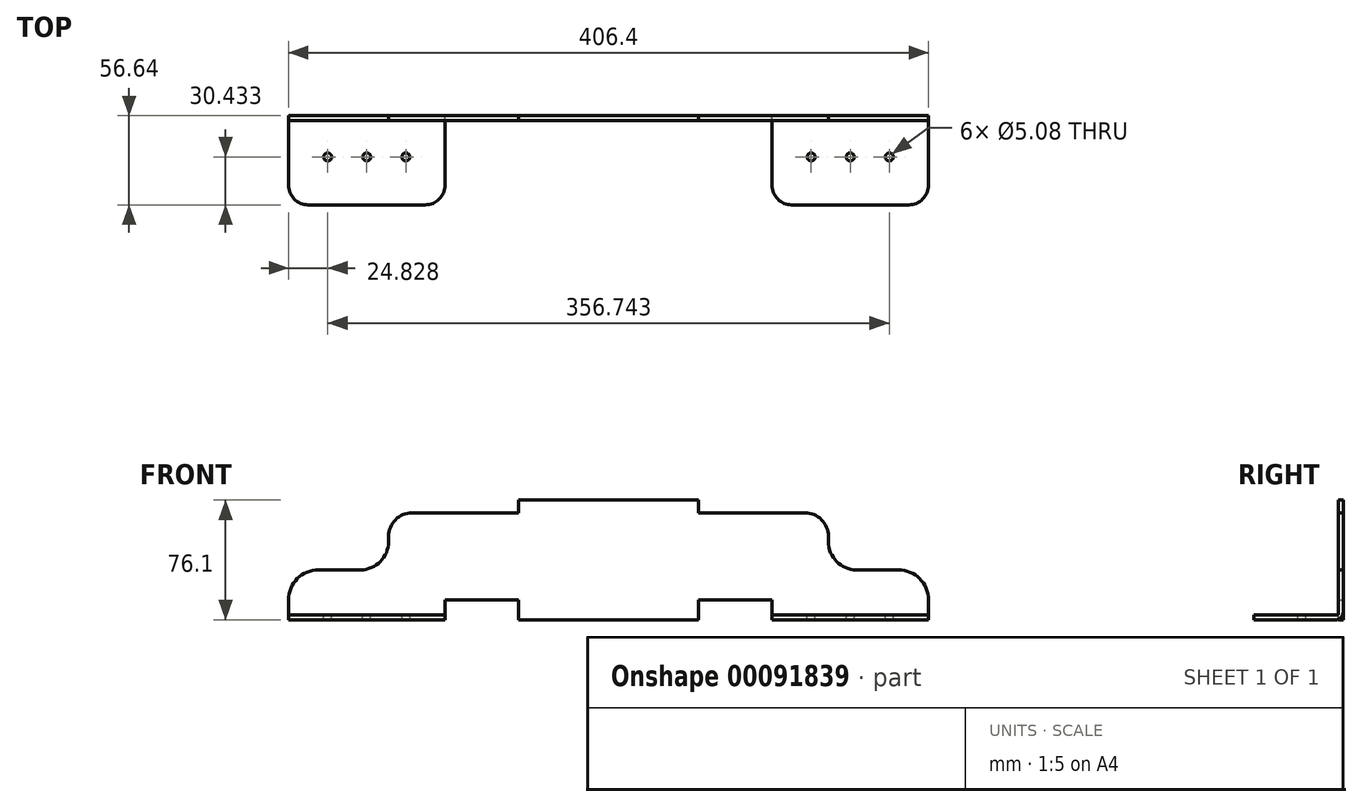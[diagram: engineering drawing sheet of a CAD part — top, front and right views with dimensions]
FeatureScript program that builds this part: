
annotation { "Feature Type Name" : "Feature", "Feature Type Description" : "" }
export const myFeature = defineFeature(function(context is Context, id is Id, definition is map)
    precondition{}
    {
        {
            var Q0;
            Q0=qCreatedBy(makeId("Front.planeOp"),FACE);
            var sketch = newSketch(context, id + "F0", { "sketchPlane" : qUnion([Q0])});
            skLineSegment(sketch, "E0.bottom", {"start": v(0, 0) * mm, "end": v(-57.15, 0) * mm});
            skLineSegment(sketch, "E0.top", {"start": v(0, 40.34) * mm, "end": v(-57.15, 40.34) * mm});
            skLineSegment(sketch, "E0.left", {"start": v(0, 0) * mm, "end": v(0, 40.34) * mm});
            skLineSegment(sketch, "E0.right", {"start": v(-57.15, 0) * mm, "end": v(-57.15, 40.34) * mm});
            skLineSegment(sketch, "E1.bottom", {"start": v(-57.15, 40.34) * mm, "end": v(-103.89, 40.34) * mm});
            skLineSegment(sketch, "E1.top", {"start": v(-57.15, 12.7) * mm, "end": v(-103.89, 12.7) * mm});
            skLineSegment(sketch, "E1.left", {"start": v(-57.15, 40.34) * mm, "end": v(-57.15, 12.7) * mm});
            skLineSegment(sketch, "E1.right", {"start": v(-103.89, 40.34) * mm, "end": v(-103.89, 12.7) * mm});
            skLineSegment(sketch, "E2.MirrorCS", {"start": v(-103.89, 40.34) * mm, "end": v(-103.89, 67.97) * mm});
            skLineSegment(sketch, "E3.MirrorCS", {"start": v(-57.15, 67.97) * mm, "end": v(-103.89, 67.97) * mm});
            skLineSegment(sketch, "E4.MirrorCS", {"start": v(-57.15, 40.34) * mm, "end": v(-57.15, 67.97) * mm});
            skLineSegment(sketch, "E5.bottom", {"start": v(-103.89, 67.97) * mm, "end": v(-139.7, 67.97) * mm});
            skLineSegment(sketch, "E5.top", {"start": v(-103.89, 0) * mm, "end": v(-139.7, 0) * mm});
            skLineSegment(sketch, "E5.left", {"start": v(-103.89, 67.97) * mm, "end": v(-103.89, 0) * mm});
            skLineSegment(sketch, "E6.bottom", {"start": v(-139.7, 0) * mm, "end": v(-203.2, 0) * mm});
            skLineSegment(sketch, "E6.top", {"start": v(-139.7, 31.75) * mm, "end": v(-203.2, 31.75) * mm});
            skLineSegment(sketch, "E6.left", {"start": v(-139.7, 0) * mm, "end": v(-139.7, 31.75) * mm});
            skLineSegment(sketch, "E6.right", {"start": v(-203.2, 0) * mm, "end": v(-203.2, 31.75) * mm});
            skLineSegment(sketch, "E7", {"start": v(-57.15, 67.97) * mm, "end": v(0, 67.97) * mm});
            skLineSegment(sketch, "E8", {"start": v(0, 67.97) * mm, "end": v(0, 40.34) * mm});
            skLineSegment(sketch, "E9", {"start": v(-57.15, 67.97) * mm, "end": v(-57.15, 76.1) * mm});
            skLineSegment(sketch, "E10", {"start": v(-57.15, 76.1) * mm, "end": v(0, 76.1) * mm});
            skLineSegment(sketch, "E11", {"start": v(0, 76.1) * mm, "end": v(0, 67.97) * mm});
            skLineSegment(sketch, "E12", {"start": v(-139.7, 67.97) * mm, "end": v(-139.7, 31.75) * mm});
            skLineSegment(sketch, "E13", {"start": v(-103.89, 3.18) * mm, "end": v(-203.2, 3.18) * mm});
            skLineSegment(sketch, "E14", {"start": v(-203.2, 3.18) * mm, "end": v(-203.2, 0) * mm});
            skSolve(sketch);
        }
        {
            var Q0;
            {var subQ0=sQuery(id+"F0.wireOp",EDGE,"E6.top");Q0=makeQuery(id+"F0.imprint","IMPRINT",FACE,{"disambiguationData":[TD([[makeQuery(id+"F0.imprint","IMPRINT",EDGE,{"derivedFrom":subQ0}),1.0]])]});}
            var Q1;
            {var subQ0=sQuery(id+"F0.wireOp",EDGE,"2503e86a-e470-4966-b1d1-eb231d9cc19f15.MirrorCS");Q1=makeQuery(id+"F0.imprint","IMPRINT",FACE,{"disambiguationData":[TD([[makeQuery(id+"F0.imprint","IMPRINT",EDGE,{"derivedFrom":subQ0}),-1.0]])]});}
            var Q2;
            Q2=makeQuery(id+"F0.imprint","IMPRINT",FACE,{"disambiguationData":[TD([[makeQuery(id+"F0.imprint","IMPRINT",EDGE,{"derivedFrom":sQuery(id+"F0.wireOp",EDGE,"E0.bottom")}),-1.0]])]});
            var Q3;
            {var subQ0=sQuery(id+"F0.wireOp",EDGE,"E1.bottom");Q3=makeQuery(id+"F0.imprint","IMPRINT",FACE,{"disambiguationData":[TD([[makeQuery(id+"F0.imprint","IMPRINT",EDGE,{"derivedFrom":subQ0}),1.0]])]});}
            var Q4;
            {var subQ0=sQuery(id+"F0.wireOp",EDGE,"E1.bottom");Q4=makeQuery(id+"F0.imprint","IMPRINT",FACE,{"disambiguationData":[TD([[makeQuery(id+"F0.imprint","IMPRINT",EDGE,{"derivedFrom":subQ0}),-1.0]])]});}
            var Q5;
            Q5=makeQuery(id+"F0.imprint","IMPRINT",FACE,{"disambiguationData":[TD([[makeQuery(id+"F0.imprint","IMPRINT",EDGE,{"derivedFrom":sQuery(id+"F0.wireOp",EDGE,"d7e3aea6-42ce-4507-9b3a-23066b92194c1.MirrorCS")}),-1.0]])]});
            var Q6;
            Q6=makeQuery(id+"F0.imprint","IMPRINT",FACE,{"disambiguationData":[TD([[makeQuery(id+"F0.imprint","IMPRINT",EDGE,{"derivedFrom":sQuery(id+"F0.wireOp",EDGE,"d7e3aea6-42ce-4507-9b3a-23066b92194c1.MirrorCS")}),1.0]])]});
            var Q7;
            Q7=makeQuery(id+"F0.imprint","IMPRINT",FACE,{"disambiguationData":[TD([[makeQuery(id+"F0.imprint","IMPRINT",EDGE,{"derivedFrom":sQuery(id+"F0.wireOp",EDGE,"2503e86a-e470-4966-b1d1-eb231d9cc19f5.MirrorCS")}),1.0]])]});
            var Q8;
            {var subQ0=sQuery(id+"F0.wireOp",EDGE,"2503e86a-e470-4966-b1d1-eb231d9cc19f10.MirrorCS");Q8=makeQuery(id+"F0.imprint","IMPRINT",FACE,{"disambiguationData":[TD([[makeQuery(id+"F0.imprint","IMPRINT",EDGE,{"derivedFrom":subQ0}),-1.0]])]});}
            var Q9;
            Q9=makeQuery(id+"F0.imprint","IMPRINT",FACE,{"disambiguationData":[TD([[makeQuery(id+"F0.imprint","IMPRINT",EDGE,{"derivedFrom":sQuery(id+"F0.wireOp",EDGE,"2503e86a-e470-4966-b1d1-eb231d9cc19f17.MirrorCS")}),-1.0]])]});
            var Q10;
            {var subQ8=sQuery(id+"F0.wireOp",EDGE,"E5.bottom");Q10=makeQuery(id+"F0.imprint","IMPRINT",FACE,{"disambiguationData":[TD([[makeQuery(id+"F0.imprint","IMPRINT",EDGE,{"derivedFrom":subQ8}),1.0]])]});}
            var Q11;
            {var subQ5=sQuery(id+"F0.wireOp",EDGE,"2503e86a-e470-4966-b1d1-eb231d9cc19f8.MirrorCS");Q11=makeQuery(id+"F0.imprint","IMPRINT",FACE,{"disambiguationData":[TD([[makeQuery(id+"F0.imprint","IMPRINT",EDGE,{"derivedFrom":subQ5}),-1.0]])]});}
            var Q12;
            Q12=makeQuery(id+"F0.imprint","IMPRINT",FACE,{"disambiguationData":[TD([[makeQuery(id+"F0.imprint","IMPRINT",EDGE,{"derivedFrom":sQuery(id+"F0.wireOp",EDGE,"E0.top")}),-1.0]])]});
            var Q13;
            Q13=makeQuery(id+"F0.imprint","IMPRINT",FACE,{"disambiguationData":[TD([[makeQuery(id+"F0.imprint","IMPRINT",EDGE,{"derivedFrom":sQuery(id+"F0.wireOp",EDGE,"E7")}),1.0]])]});
            extrude(context, id + "F1", {"entities" : qUnion([Q0, Q1, Q2, Q3, Q4, Q5, Q6, Q7, Q8, Q9, Q10, Q11, Q12, Q13]), "depth" : 3.17 * mm});
        }
        {
            var Q0;
            {var subQ5=sQuery(id+"F0.wireOp",EDGE,"5YBeUyX7-qxhe-6PBE-ShX0-8MnYnTLxuj8z.left");Q0=makeQuery(id+"F0.imprint","IMPRINT",FACE,{"disambiguationData":[TD([[makeQuery(id+"F0.imprint","IMPRINT",EDGE,{"derivedFrom":subQ5}),-1.0]])]});}
            var Q1;
            {var subQ5=sQuery(id+"F0.wireOp",EDGE,"5YBeUyX7-qxhe-6PBE-ShX0-8MnYnTLxuj8z.right");Q1=makeQuery(id+"F0.imprint","IMPRINT",FACE,{"disambiguationData":[TD([[makeQuery(id+"F0.imprint","IMPRINT",EDGE,{"derivedFrom":subQ5}),1.0]])]});}
            var Q2;
            {var subQ0=sQuery(id+"F0.wireOp",EDGE,"2503e86a-e470-4966-b1d1-eb231d9cc19f11.MirrorCS");Q2=makeQuery(id+"F0.imprint","IMPRINT",FACE,{"disambiguationData":[TD([[makeQuery(id+"F0.imprint","IMPRINT",EDGE,{"derivedFrom":subQ0}),-1.0]])]});}
            var Q3;
            {var subQ0=sQuery(id+"F0.wireOp",EDGE,"2503e86a-e470-4966-b1d1-eb231d9cc19f18.MirrorCS");Q3=makeQuery(id+"F0.imprint","IMPRINT",FACE,{"disambiguationData":[TD([[makeQuery(id+"F0.imprint","IMPRINT",EDGE,{"derivedFrom":subQ0}),1.0]])]});}
            var Q4;
            {var subQ0=sQuery(id+"F0.wireOp",EDGE,"E6.bottom");Q4=makeQuery(id+"F0.imprint","IMPRINT",FACE,{"disambiguationData":[TD([[makeQuery(id+"F0.imprint","IMPRINT",EDGE,{"derivedFrom":subQ0}),-1.0]])]});}
            var Q5;
            {var subQ0=sQuery(id+"F0.wireOp",EDGE,"E5.top");Q5=makeQuery(id+"F0.imprint","IMPRINT",FACE,{"disambiguationData":[TD([[makeQuery(id+"F0.imprint","IMPRINT",EDGE,{"derivedFrom":subQ0}),-1.0]])]});}
            extrude(context, id + "F2", {"entities" : qUnion([Q0, Q1, Q2, Q3, Q4, Q5]), "operationType" : NewBodyOperationType.ADD, "depth" : 56.64 * mm});
        }
        {
            var Q0;
            Q0=makeQuery(id+"F1.opExtrude","SWEPT_EDGE",EDGE,{"disambiguationData":[OSD([sQuery(id+"F0.wireOp",EDGE,"E6.top"),sQuery(id+"F0.wireOp",EDGE,"E6.right")])]});
            fillet(context, id + "F3", {"entities" : qUnion([Q0]), "radius" : 19 * mm, "tangentPropagation" : true, "allowEdgeOverflow" : false});
        }
        {
            var Q0;
            Q0=makeQuery(id+"F1.opExtrude","SWEPT_EDGE",EDGE,{"disambiguationData":[OSD([sQuery(id+"F0.wireOp",EDGE,"E5.right"),sQuery(id+"F0.wireOp",EDGE,"E6.top"),sQuery(id+"F0.wireOp",EDGE,"E6.left")])]});
            fillet(context, id + "F4", {"entities" : qUnion([Q0]), "radius" : 17.83 * mm, "tangentPropagation" : true, "allowEdgeOverflow" : false});
        }
        {
            var Q0;
            Q0=makeQuery(id+"F1.opExtrude","SWEPT_EDGE",EDGE,{"disambiguationData":[OSD([sQuery(id+"F0.wireOp",EDGE,"E5.bottom"),sQuery(id+"F0.wireOp",EDGE,"E5.right")])]});
            fillet(context, id + "F5", {"entities" : qUnion([Q0]), "radius" : 14.97 * mm, "tangentPropagation" : true, "allowEdgeOverflow" : false});
        }
        {
            var Q0;
            Q0=makeQuery(id+"F2.opExtrude","CAP_EDGE",EDGE,{"disambiguationData":[OSD([sQuery(id+"F0.wireOp",EDGE,"E5.top"),sQuery(id+"F0.wireOp",EDGE,"E6.bottom")])],"isStart":true});
            var Q1;
            Q1=makeQuery(id+"F1.opExtrude","CAP_EDGE",EDGE,{"disambiguationData":[OSD([sQuery(id+"F0.wireOp",EDGE,"E13")])],"isStart":false});
            fillet(context, id + "F6", {"entities" : qUnion([Q0, Q1]), "radius" : 5.08 * mm, "tangentPropagation" : true, "allowEdgeOverflow" : false});
        }
        {
            var Q0;
            Q0=makeQuery(id+"F2.opExtrude","CAP_EDGE",EDGE,{"disambiguationData":[OSD([sQuery(id+"F0.wireOp",EDGE,"5YBeUyX7-qxhe-6PBE-ShX0-8MnYnTLxuj8z.left")])],"isStart":false});
            var Q1;
            Q1=makeQuery(id+"F2.opExtrude","CAP_EDGE",EDGE,{"disambiguationData":[OSD([sQuery(id+"F0.wireOp",EDGE,"5YBeUyX7-qxhe-6PBE-ShX0-8MnYnTLxuj8z.right")])],"isStart":false});
            var Q2;
            Q2=makeQuery(id+"F2.opExtrude","CAP_EDGE",EDGE,{"disambiguationData":[OSD([sQuery(id+"F0.wireOp",EDGE,"E5.left")])],"isStart":false});
            var Q3;
            Q3=makeQuery(id+"F2.opExtrude","CAP_EDGE",EDGE,{"disambiguationData":[OSD([sQuery(id+"F0.wireOp",EDGE,"E6.right")])],"isStart":false});
            var Q4;
            Q4=makeQuery(id+"F2.opExtrude","CAP_EDGE",EDGE,{"disambiguationData":[OSD([sQuery(id+"F0.wireOp",EDGE,"E14")])],"isStart":false});
            fillet(context, id + "F7", {"entities" : qUnion([Q0, Q1, Q2, Q3, Q4]), "radius" : 12.48 * mm, "tangentPropagation" : true, "allowEdgeOverflow" : false});
        }
        {
            var Q0;
            Q0=makeQuery(id+"F2.opExtrude","SWEPT_FACE",FACE,{"disambiguationData":[OSD([sQuery(id+"F0.wireOp",EDGE,"E13")])]});
            var sketch = newSketch(context, id + "F8", { "sketchPlane" : qUnion([Q0])});
            skLineSegment(sketch, "E15", {"start": v(-103.89, -26.2) * mm, "end": v(-153.54, -26.2) * mm, "construction": true});
            skPoint(sketch, "E15.endSnap0", {"position": v(-153.54, -56.64) * mm});
            skLineSegment(sketch, "E16", {"start": v(-153.54, -26.2) * mm, "end": v(-203.2, -26.2) * mm, "construction": true});
            skPoint(sketch, "E17", {"position": v(-128.71, -26.2) * mm});
            skPoint(sketch, "E18", {"position": v(-178.37, -26.2) * mm});
            skSolve(sketch);
        }
        {
            var Q0;
            Q0=sQuery(id+"F8.wireOp",VERTEX,"E15.end");
            var Q1;
            Q1=sQuery(id+"F8.wireOp",VERTEX,"E17");
            var Q2;
            Q2=sQuery(id+"F8.wireOp",VERTEX,"E18");
            var Q3;
            Q3=makeQuery(id+"F1.opExtrude","SWEPT_BODY",BODY,{"disambiguationData":[OSD([sQuery(id+"F0.wireOp",EDGE,"E0.bottom"),sQuery(id+"F0.wireOp",EDGE,"E0.right"),sQuery(id+"F0.wireOp",EDGE,"E1.top"),sQuery(id+"F0.wireOp",EDGE,"d7e3aea6-42ce-4507-9b3a-23066b92194c1.MirrorCS"),sQuery(id+"F0.wireOp",EDGE,"d7e3aea6-42ce-4507-9b3a-23066b92194c2.MirrorCS"),sQuery(id+"F0.wireOp",EDGE,"E3.MirrorCS"),sQuery(id+"F0.wireOp",EDGE,"d7e3aea6-42ce-4507-9b3a-23066b92194c4.MirrorCS"),sQuery(id+"F0.wireOp",EDGE,"E5.bottom"),sQuery(id+"F0.wireOp",EDGE,"E5.left"),sQuery(id+"F0.wireOp",EDGE,"E5.right"),sQuery(id+"F0.wireOp",EDGE,"E6.top"),sQuery(id+"F0.wireOp",EDGE,"E6.right"),sQuery(id+"F0.wireOp",EDGE,"5YBeUyX7-qxhe-6PBE-ShX0-8MnYnTLxuj8z.top"),sQuery(id+"F0.wireOp",EDGE,"E0.left")])]});
            hole(context, id + "F9", {"style" : HoleStyle.SIMPLE, "endStyle" : HoleEndStyle.BLIND, "holeDiameter" : 5.08 * mm, "holeDepth" : 25.4 * mm, "locations" : qUnion([Q0, Q1, Q2]), "scope" : qUnion([Q3])});
        }
        {
            var Q0;
            Q0=makeQuery(id+"F1.opExtrude","SWEPT_BODY",BODY,{"disambiguationData":[OSD([sQuery(id+"F0.wireOp",EDGE,"E0.bottom"),sQuery(id+"F0.wireOp",EDGE,"E0.right"),sQuery(id+"F0.wireOp",EDGE,"E1.top"),sQuery(id+"F0.wireOp",EDGE,"d7e3aea6-42ce-4507-9b3a-23066b92194c1.MirrorCS"),sQuery(id+"F0.wireOp",EDGE,"d7e3aea6-42ce-4507-9b3a-23066b92194c2.MirrorCS"),sQuery(id+"F0.wireOp",EDGE,"E3.MirrorCS"),sQuery(id+"F0.wireOp",EDGE,"d7e3aea6-42ce-4507-9b3a-23066b92194c4.MirrorCS"),sQuery(id+"F0.wireOp",EDGE,"E5.bottom"),sQuery(id+"F0.wireOp",EDGE,"E5.left"),sQuery(id+"F0.wireOp",EDGE,"E5.right"),sQuery(id+"F0.wireOp",EDGE,"E6.top"),sQuery(id+"F0.wireOp",EDGE,"E6.right"),sQuery(id+"F0.wireOp",EDGE,"5YBeUyX7-qxhe-6PBE-ShX0-8MnYnTLxuj8z.top"),sQuery(id+"F0.wireOp",EDGE,"E0.left")])]});
            var Q1;
            Q1=makeQuery(id+"F1.opExtrude","SWEPT_FACE",FACE,{"disambiguationData":[OSD([sQuery(id+"F0.wireOp",EDGE,"d7e3aea6-42ce-4507-9b3a-23066b92194c1.MirrorCS"),sQuery(id+"F0.wireOp",EDGE,"E0.left")])]});
            mirror(context, id + "F10", {"operationType" : NewBodyOperationType.ADD, "entities" : qUnion([Q0]), "mirrorPlane" : qUnion([Q1])});
        }
    });
